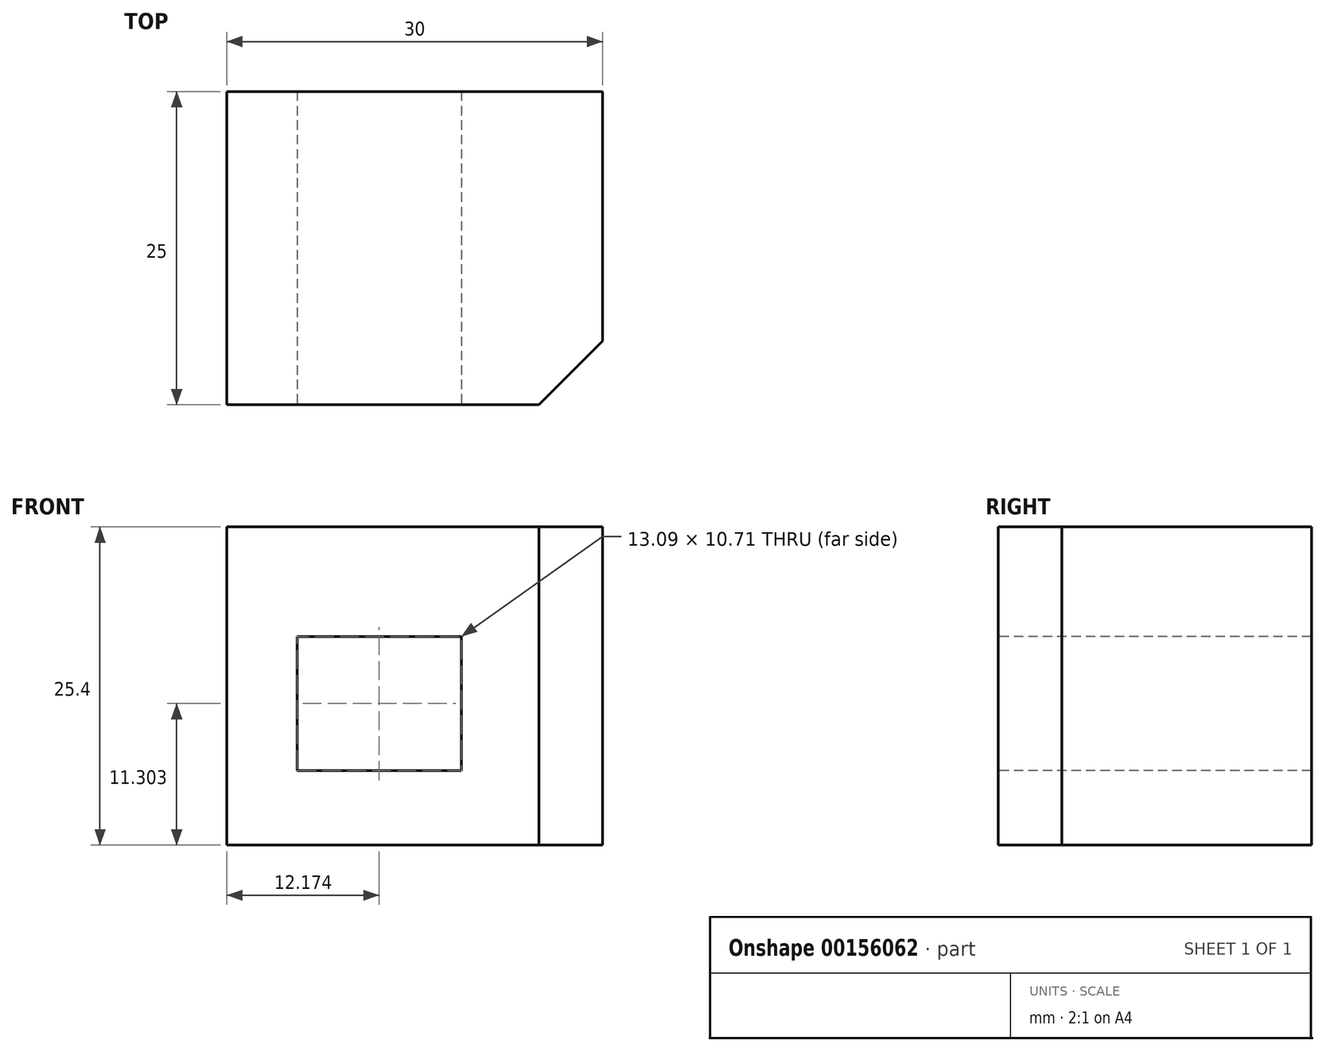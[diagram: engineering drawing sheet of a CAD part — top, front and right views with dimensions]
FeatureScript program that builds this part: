
annotation { "Feature Type Name" : "Feature", "Feature Type Description" : "" }
export const myFeature = defineFeature(function(context is Context, id is Id, definition is map)
    precondition{}
    {
        {
            var Q0;
            Q0=qCreatedBy(makeId("Top.planeOp"),FACE);
            var sketch = newSketch(context, id + "F0", { "sketchPlane" : qUnion([Q0])});
            skLineSegment(sketch, "E0.bottom", {"start": v(-5.63, 13.74) * mm, "end": v(24.37, 13.74) * mm});
            skLineSegment(sketch, "E0.top", {"start": v(-5.63, -11.26) * mm, "end": v(24.37, -11.26) * mm});
            skLineSegment(sketch, "E0.left", {"start": v(-5.63, 13.74) * mm, "end": v(-5.63, -11.26) * mm});
            skLineSegment(sketch, "E0.right", {"start": v(24.37, 13.74) * mm, "end": v(24.37, -11.26) * mm});
            skSolve(sketch);
        }
        {
            var Q0;
            Q0=makeQuery(id+"F0.imprint","IMPRINT",FACE,{"disambiguationData":[TD([[makeQuery(id+"F0.imprint","IMPRINT",EDGE,{"derivedFrom":sQuery(id+"F0.wireOp",EDGE,"E0.bottom")}),-1.0]])]});
            extrude(context, id + "F1", {"entities" : qUnion([Q0]), "depth" : 25.4 * mm});
        }
        {
            var Q0;
            Q0=makeQuery(id+"F1.opExtrude","SWEPT_EDGE",EDGE,{"disambiguationData":[OSD([sQuery(id+"F0.wireOp",EDGE,"E0.top"),sQuery(id+"F0.wireOp",EDGE,"E0.right")])]});
            chamfer(context, id + "F2", {"entities" : qUnion([Q0]), "width" : 5.08 * mm, "tangentPropagation" : true});
        }
        {
            var Q0;
            Q0=makeQuery(id+"F1.opExtrude","SWEPT_FACE",FACE,{"disambiguationData":[OSD([sQuery(id+"F0.wireOp",EDGE,"E0.top")])]});
            var sketch = newSketch(context, id + "F3", { "sketchPlane" : qUnion([Q0])});
            skLineSegment(sketch, "E1.bottom", {"start": v(0, 16.66) * mm, "end": v(13.09, 16.66) * mm});
            skLineSegment(sketch, "E1.top", {"start": v(0, 5.95) * mm, "end": v(13.09, 5.95) * mm});
            skLineSegment(sketch, "E1.left", {"start": v(0, 16.66) * mm, "end": v(0, 5.95) * mm});
            skLineSegment(sketch, "E1.right", {"start": v(13.09, 16.66) * mm, "end": v(13.09, 5.95) * mm});
            skSolve(sketch);
        }
        {
            var Q0;
            Q0=makeQuery(id+"F3.imprint","IMPRINT",FACE,{"disambiguationData":[TD([[makeQuery(id+"F3.imprint","IMPRINT",EDGE,{"derivedFrom":sQuery(id+"F3.wireOp",EDGE,"E1.bottom")}),-1.0]])]});
            extrude(context, id + "F4", {"entities" : qUnion([Q0]), "operationType" : NewBodyOperationType.REMOVE, "oppositeDirection" : true, "depth" : 35.94 * mm});
        }
    });
